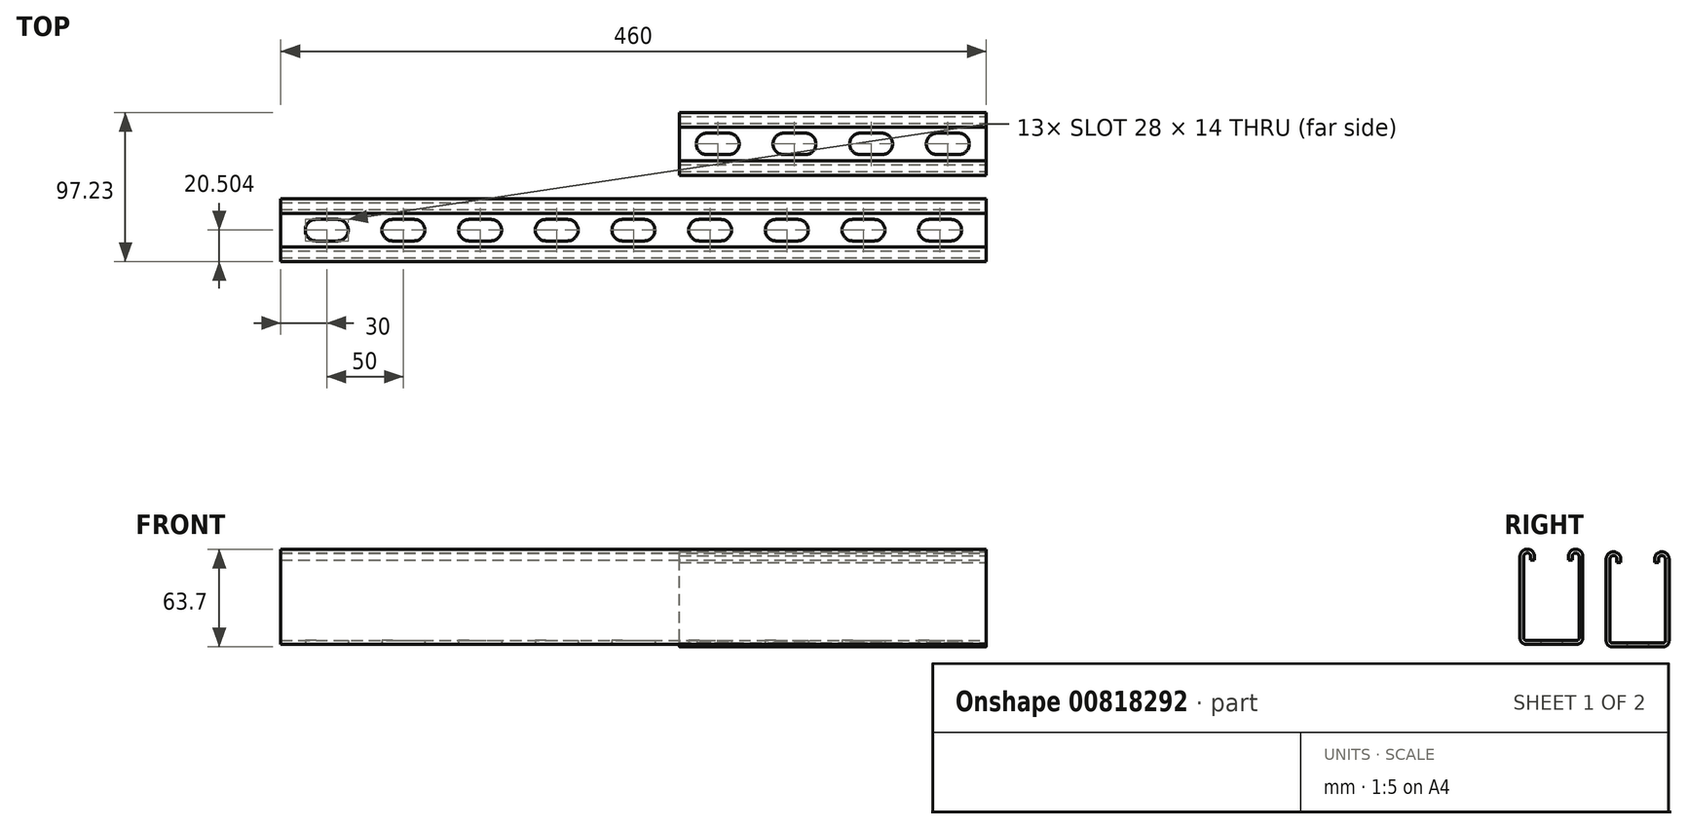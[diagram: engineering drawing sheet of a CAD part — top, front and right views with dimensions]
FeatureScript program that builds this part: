
annotation { "Feature Type Name" : "Feature", "Feature Type Description" : "" }
export const myFeature = defineFeature(function(context is Context, id is Id, definition is map)
    precondition{}
    {
        {
            var Q0;
            Q0=qCreatedBy(makeId("Right.planeOp"),FACE);
            var sketch = newSketch(context, id + "F0", { "sketchPlane" : qUnion([Q0])});
            skLineSegment(sketch, "E0", {"start": v(0, 4) * mm, "end": v(0, 57.25) * mm});
            skLineSegment(sketch, "E1", {"start": v(4, 0) * mm, "end": v(37, 0) * mm});
            skLineSegment(sketch, "E2", {"start": v(41, 4) * mm, "end": v(41, 57.25) * mm});
            skLineSegment(sketch, "E3", {"start": v(9.5, 57.25) * mm, "end": v(9.5, 54.9) * mm});
            skLineSegment(sketch, "E4", {"start": v(31.56, 57.25) * mm, "end": v(31.56, 54.9) * mm});
            skPoint(sketch, "E5.visualSharp", {"position": v(0, 0) * mm});
            skArc(sketch, "E5.filletArc", {"start": v(0, 4) * mm, "mid": v(1.17, 1.17) * mm, "end": v(4, 0) * mm});
            skPoint(sketch, "E6.visualSharp", {"position": v(41, 0) * mm});
            skArc(sketch, "E6.filletArc", {"start": v(37, 0) * mm, "mid": v(39.83, 1.17) * mm, "end": v(41, 4) * mm});
            skArc(sketch, "E7", {"start": v(9.5, 57.25) * mm, "mid": v(4.75, 62) * mm, "end": v(0, 57.25) * mm});
            skPoint(sketch, "E8.orphan", {"position": v(0, 62) * mm});
            skArc(sketch, "E9.MirrorCS", {"start": v(31.56, 57.25) * mm, "mid": v(36.28, 61.97) * mm, "end": v(41, 57.25) * mm});
            skPoint(sketch, "E10.orphan", {"position": v(41, 62) * mm});
            skPoint(sketch, "E11.orphan", {"position": v(31.56, 62) * mm});
            skPoint(sketch, "E12.start.orphan", {"position": v(9.5, 62) * mm});
            skPoint(sketch, "E13.start.orphan", {"position": v(20.53, 62) * mm});
            skLineSegment(sketch, "E14.0", {"start": v(7, 57.25) * mm, "end": v(7, 54.9) * mm});
            skArc(sketch, "E14.1", {"start": v(7, 57.25) * mm, "mid": v(4.75, 59.5) * mm, "end": v(2.5, 57.25) * mm});
            skLineSegment(sketch, "E14.2", {"start": v(2.5, 4) * mm, "end": v(2.5, 57.25) * mm});
            skArc(sketch, "E14.3", {"start": v(2.5, 4) * mm, "mid": v(2.94, 2.94) * mm, "end": v(4, 2.5) * mm});
            skLineSegment(sketch, "E14.4", {"start": v(4, 2.5) * mm, "end": v(37, 2.5) * mm});
            skLineSegment(sketch, "E14.5", {"start": v(34.06, 57.25) * mm, "end": v(34.06, 54.9) * mm});
            skArc(sketch, "E14.6", {"start": v(34.06, 57.25) * mm, "mid": v(36.28, 59.47) * mm, "end": v(38.5, 57.25) * mm});
            skLineSegment(sketch, "E14.7", {"start": v(38.5, 4) * mm, "end": v(38.5, 57.25) * mm});
            skArc(sketch, "E14.8", {"start": v(37, 2.5) * mm, "mid": v(38.06, 2.94) * mm, "end": v(38.5, 4) * mm});
            skLineSegment(sketch, "E15", {"start": v(7, 54.9) * mm, "end": v(9.5, 54.9) * mm});
            skLineSegment(sketch, "E16", {"start": v(31.56, 54.9) * mm, "end": v(34.06, 54.9) * mm});
            skSolve(sketch);
        }
        {
            var Q0;
            Q0 = qSketchRegion(id + "F0", true);
            extrude(context, id + "F1", {"entities" : qUnion([Q0]), "oppositeDirection" : true, "depth" : 200 * mm, "offsetDistance" : 25 * mm});
        }
        {
            var Q0;
            Q0=makeQuery(id+"F1.opExtrude","SWEPT_FACE",FACE,{"disambiguationData":[OSD([sQuery(id+"F0.wireOp",EDGE,"E1")])]});
            var sketch = newSketch(context, id + "F2", { "sketchPlane" : qUnion([Q0])});
            skLineSegment(sketch, "E17", {"start": v(0, -20.5) * mm, "end": v(-200, -20.5) * mm, "construction": true});
            skLineSegment(sketch, "E18.bottom", {"start": v(-118, -13.5) * mm, "end": v(-132, -13.5) * mm});
            skLineSegment(sketch, "E18.top", {"start": v(-118, -27.5) * mm, "end": v(-132, -27.5) * mm});
            skPoint(sketch, "E18.middle", {"position": v(-125, -20.5) * mm});
            skArc(sketch, "E19", {"start": v(-118, -27.5) * mm, "mid": v(-111, -20.5) * mm, "end": v(-118, -13.5) * mm});
            skArc(sketch, "E20", {"start": v(-132, -13.5) * mm, "mid": v(-139, -20.5) * mm, "end": v(-132, -27.5) * mm});
            skPoint(sketch, "E21.orphan", {"position": v(-111, -13.5) * mm});
            skPoint(sketch, "E22.orphan", {"position": v(-139, -13.5) * mm});
            skPoint(sketch, "E23.orphan", {"position": v(-139, -27.5) * mm});
            skPoint(sketch, "E18.left.end.orphan", {"position": v(-111, -27.5) * mm});
            skArc(sketch, "E24.1.0.0", {"start": v(-68, -27.5) * mm, "mid": v(-61, -20.5) * mm, "end": v(-68, -13.5) * mm});
            skLineSegment(sketch, "E24.1.0.1", {"start": v(-68, -13.5) * mm, "end": v(-82, -13.5) * mm});
            skArc(sketch, "E24.1.0.2", {"start": v(-82, -13.5) * mm, "mid": v(-89, -20.5) * mm, "end": v(-82, -27.5) * mm});
            skLineSegment(sketch, "E24.1.0.3", {"start": v(-68, -27.5) * mm, "end": v(-82, -27.5) * mm});
            skArc(sketch, "E24.2.0.0", {"start": v(-18, -27.5) * mm, "mid": v(-11, -20.5) * mm, "end": v(-18, -13.5) * mm});
            skLineSegment(sketch, "E24.2.0.1", {"start": v(-18, -13.5) * mm, "end": v(-32, -13.5) * mm});
            skArc(sketch, "E24.2.0.2", {"start": v(-32, -13.5) * mm, "mid": v(-39, -20.5) * mm, "end": v(-32, -27.5) * mm});
            skLineSegment(sketch, "E24.2.0.3", {"start": v(-18, -27.5) * mm, "end": v(-32, -27.5) * mm});
            skLineSegment(sketch, "E25.1.0.0", {"start": v(-168, -27.5) * mm, "end": v(-182, -27.5) * mm});
            skArc(sketch, "E25.1.0.1", {"start": v(-168, -27.5) * mm, "mid": v(-161, -20.5) * mm, "end": v(-168, -13.5) * mm});
            skLineSegment(sketch, "E25.1.0.2", {"start": v(-168, -13.5) * mm, "end": v(-182, -13.5) * mm});
            skArc(sketch, "E25.1.0.3", {"start": v(-182, -13.5) * mm, "mid": v(-189, -20.5) * mm, "end": v(-182, -27.5) * mm});
            skSolve(sketch);
        }
        {
            var Q0;
            Q0 = qSketchRegion(id + "F2", true);
            extrude(context, id + "F3", {"entities" : qUnion([Q0]), "operationType" : NewBodyOperationType.REMOVE, "oppositeDirection" : true, "depth" : 25 * mm, "offsetDistance" : 25 * mm});
        }
        {
            var Q0;
            Q0=qCreatedBy(makeId("Right.planeOp"),FACE);
            var sketch = newSketch(context, id + "F4", { "sketchPlane" : qUnion([Q0])});
            skLineSegment(sketch, "E26", {"start": v(-56.23, 5.7) * mm, "end": v(-56.23, 58.95) * mm});
            skLineSegment(sketch, "E27", {"start": v(-52.23, 1.7) * mm, "end": v(-19.23, 1.7) * mm});
            skLineSegment(sketch, "E28", {"start": v(-15.23, 5.7) * mm, "end": v(-15.23, 58.95) * mm});
            skLineSegment(sketch, "E29", {"start": v(-46.73, 58.95) * mm, "end": v(-46.73, 56.6) * mm});
            skLineSegment(sketch, "E30", {"start": v(-24.66, 58.95) * mm, "end": v(-24.66, 56.6) * mm});
            skPoint(sketch, "E31.visualSharp", {"position": v(-56.23, 1.7) * mm});
            skArc(sketch, "E31.filletArc", {"start": v(-56.23, 5.7) * mm, "mid": v(-55.05, 2.87) * mm, "end": v(-52.23, 1.7) * mm});
            skPoint(sketch, "E32.visualSharp", {"position": v(-15.23, 1.7) * mm});
            skArc(sketch, "E32.filletArc", {"start": v(-19.23, 1.7) * mm, "mid": v(-16.4, 2.87) * mm, "end": v(-15.23, 5.7) * mm});
            skArc(sketch, "E33", {"start": v(-46.73, 58.95) * mm, "mid": v(-51.48, 63.7) * mm, "end": v(-56.23, 58.95) * mm});
            skPoint(sketch, "E34.orphan", {"position": v(-56.23, 63.7) * mm});
            skArc(sketch, "E35.MirrorCS", {"start": v(-24.66, 58.95) * mm, "mid": v(-19.94, 63.67) * mm, "end": v(-15.23, 58.95) * mm});
            skPoint(sketch, "E36.orphan", {"position": v(-15.23, 63.7) * mm});
            skPoint(sketch, "E37.orphan", {"position": v(-24.66, 63.7) * mm});
            skPoint(sketch, "E38.start.orphan", {"position": v(-46.73, 63.7) * mm});
            skPoint(sketch, "E39.start.orphan", {"position": v(-35.7, 63.7) * mm});
            skLineSegment(sketch, "E40.0", {"start": v(-49.23, 58.95) * mm, "end": v(-49.23, 56.6) * mm});
            skArc(sketch, "E40.1", {"start": v(-49.23, 58.95) * mm, "mid": v(-51.48, 61.2) * mm, "end": v(-53.73, 58.95) * mm});
            skLineSegment(sketch, "E40.2", {"start": v(-53.73, 5.7) * mm, "end": v(-53.73, 58.95) * mm});
            skArc(sketch, "E40.3", {"start": v(-53.73, 5.7) * mm, "mid": v(-53.29, 4.64) * mm, "end": v(-52.23, 4.2) * mm});
            skLineSegment(sketch, "E40.4", {"start": v(-52.23, 4.2) * mm, "end": v(-19.23, 4.2) * mm});
            skLineSegment(sketch, "E40.5", {"start": v(-22.16, 58.95) * mm, "end": v(-22.16, 56.6) * mm});
            skArc(sketch, "E40.6", {"start": v(-22.16, 58.95) * mm, "mid": v(-19.94, 61.17) * mm, "end": v(-17.73, 58.95) * mm});
            skLineSegment(sketch, "E40.7", {"start": v(-17.73, 5.7) * mm, "end": v(-17.73, 58.95) * mm});
            skArc(sketch, "E40.8", {"start": v(-19.23, 4.2) * mm, "mid": v(-18.16, 4.64) * mm, "end": v(-17.73, 5.7) * mm});
            skLineSegment(sketch, "E41", {"start": v(-49.23, 56.6) * mm, "end": v(-46.73, 56.6) * mm});
            skLineSegment(sketch, "E42", {"start": v(-24.66, 56.6) * mm, "end": v(-22.16, 56.6) * mm});
            skSolve(sketch);
        }
        {
            var Q0;
            Q0 = qSketchRegion(id + "F4", true);
            extrude(context, id + "F5", {"entities" : qUnion([Q0]), "oppositeDirection" : true, "depth" : 460 * mm, "offsetDistance" : 25 * mm});
        }
        {
            var Q0;
            Q0=makeQuery(id+"F5.opExtrude","SWEPT_FACE",FACE,{"disambiguationData":[OSD([sQuery(id+"F4.wireOp",EDGE,"E27")])]});
            var sketch = newSketch(context, id + "F6", { "sketchPlane" : qUnion([Q0])});
            skLineSegment(sketch, "E43", {"start": v(0, 35.73) * mm, "end": v(-460, 35.73) * mm, "construction": true});
            skArc(sketch, "E44", {"start": v(-23, 28.73) * mm, "mid": v(-16, 35.73) * mm, "end": v(-23, 42.73) * mm});
            skArc(sketch, "E45", {"start": v(-37, 42.73) * mm, "mid": v(-44, 35.73) * mm, "end": v(-37, 28.73) * mm});
            skLineSegment(sketch, "E46", {"start": v(-37, 28.73) * mm, "end": v(-23, 28.73) * mm});
            skLineSegment(sketch, "E47", {"start": v(-37, 42.73) * mm, "end": v(-23, 42.73) * mm});
            skArc(sketch, "E48.1.0.0", {"start": v(-87, 42.73) * mm, "mid": v(-94, 35.73) * mm, "end": v(-87, 28.73) * mm});
            skLineSegment(sketch, "E48.1.0.1", {"start": v(-87, 28.73) * mm, "end": v(-73, 28.73) * mm});
            skArc(sketch, "E48.1.0.2", {"start": v(-73, 28.73) * mm, "mid": v(-66, 35.73) * mm, "end": v(-73, 42.73) * mm});
            skLineSegment(sketch, "E48.1.0.3", {"start": v(-87, 42.73) * mm, "end": v(-73, 42.73) * mm});
            skArc(sketch, "E48.2.0.0", {"start": v(-137, 42.73) * mm, "mid": v(-144, 35.73) * mm, "end": v(-137, 28.73) * mm});
            skLineSegment(sketch, "E48.2.0.1", {"start": v(-137, 28.73) * mm, "end": v(-123, 28.73) * mm});
            skArc(sketch, "E48.2.0.2", {"start": v(-123, 28.73) * mm, "mid": v(-116, 35.73) * mm, "end": v(-123, 42.73) * mm});
            skLineSegment(sketch, "E48.2.0.3", {"start": v(-137, 42.73) * mm, "end": v(-123, 42.73) * mm});
            skLineSegment(sketch, "E48.direction1", {"start": v(-37, 28.73) * mm, "end": v(-87, 28.73) * mm, "construction": true});
            skArc(sketch, "E49.0.3.0", {"start": v(-187, 42.73) * mm, "mid": v(-194, 35.73) * mm, "end": v(-187, 28.73) * mm});
            skLineSegment(sketch, "E49.4.3.0", {"start": v(-187, 28.73) * mm, "end": v(-173, 28.73) * mm});
            skArc(sketch, "E49.7.3.0", {"start": v(-173, 28.73) * mm, "mid": v(-166, 35.73) * mm, "end": v(-173, 42.73) * mm});
            skLineSegment(sketch, "E49.11.3.0", {"start": v(-187, 42.73) * mm, "end": v(-173, 42.73) * mm});
            skArc(sketch, "E49.0.4.0", {"start": v(-237, 42.73) * mm, "mid": v(-244, 35.73) * mm, "end": v(-237, 28.73) * mm});
            skLineSegment(sketch, "E49.4.4.0", {"start": v(-237, 28.73) * mm, "end": v(-223, 28.73) * mm});
            skArc(sketch, "E49.7.4.0", {"start": v(-223, 28.73) * mm, "mid": v(-216, 35.73) * mm, "end": v(-223, 42.73) * mm});
            skLineSegment(sketch, "E49.11.4.0", {"start": v(-237, 42.73) * mm, "end": v(-223, 42.73) * mm});
            skArc(sketch, "E49.0.5.0", {"start": v(-287, 42.73) * mm, "mid": v(-294, 35.73) * mm, "end": v(-287, 28.73) * mm});
            skLineSegment(sketch, "E49.4.5.0", {"start": v(-287, 28.73) * mm, "end": v(-273, 28.73) * mm});
            skArc(sketch, "E49.7.5.0", {"start": v(-273, 28.73) * mm, "mid": v(-266, 35.73) * mm, "end": v(-273, 42.73) * mm});
            skLineSegment(sketch, "E49.11.5.0", {"start": v(-287, 42.73) * mm, "end": v(-273, 42.73) * mm});
            skArc(sketch, "E49.0.6.0", {"start": v(-337, 42.73) * mm, "mid": v(-344, 35.73) * mm, "end": v(-337, 28.73) * mm});
            skLineSegment(sketch, "E49.4.6.0", {"start": v(-337, 28.73) * mm, "end": v(-323, 28.73) * mm});
            skArc(sketch, "E49.7.6.0", {"start": v(-323, 28.73) * mm, "mid": v(-316, 35.73) * mm, "end": v(-323, 42.73) * mm});
            skLineSegment(sketch, "E49.11.6.0", {"start": v(-337, 42.73) * mm, "end": v(-323, 42.73) * mm});
            skArc(sketch, "E49.0.7.0", {"start": v(-387, 42.73) * mm, "mid": v(-394, 35.73) * mm, "end": v(-387, 28.73) * mm});
            skLineSegment(sketch, "E49.4.7.0", {"start": v(-387, 28.73) * mm, "end": v(-373, 28.73) * mm});
            skArc(sketch, "E49.7.7.0", {"start": v(-373, 28.73) * mm, "mid": v(-366, 35.73) * mm, "end": v(-373, 42.73) * mm});
            skLineSegment(sketch, "E49.11.7.0", {"start": v(-387, 42.73) * mm, "end": v(-373, 42.73) * mm});
            skArc(sketch, "E49.0.8.0", {"start": v(-437, 42.73) * mm, "mid": v(-444, 35.73) * mm, "end": v(-437, 28.73) * mm});
            skLineSegment(sketch, "E49.4.8.0", {"start": v(-437, 28.73) * mm, "end": v(-423, 28.73) * mm});
            skArc(sketch, "E49.7.8.0", {"start": v(-423, 28.73) * mm, "mid": v(-416, 35.73) * mm, "end": v(-423, 42.73) * mm});
            skLineSegment(sketch, "E49.11.8.0", {"start": v(-437, 42.73) * mm, "end": v(-423, 42.73) * mm});
            skSolve(sketch);
        }
        {
            var Q0;
            Q0 = qSketchRegion(id + "F6", true);
            extrude(context, id + "F7", {"entities" : qUnion([Q0]), "operationType" : NewBodyOperationType.REMOVE, "oppositeDirection" : true, "depth" : 25 * mm, "offsetDistance" : 25 * mm});
        }
    });
